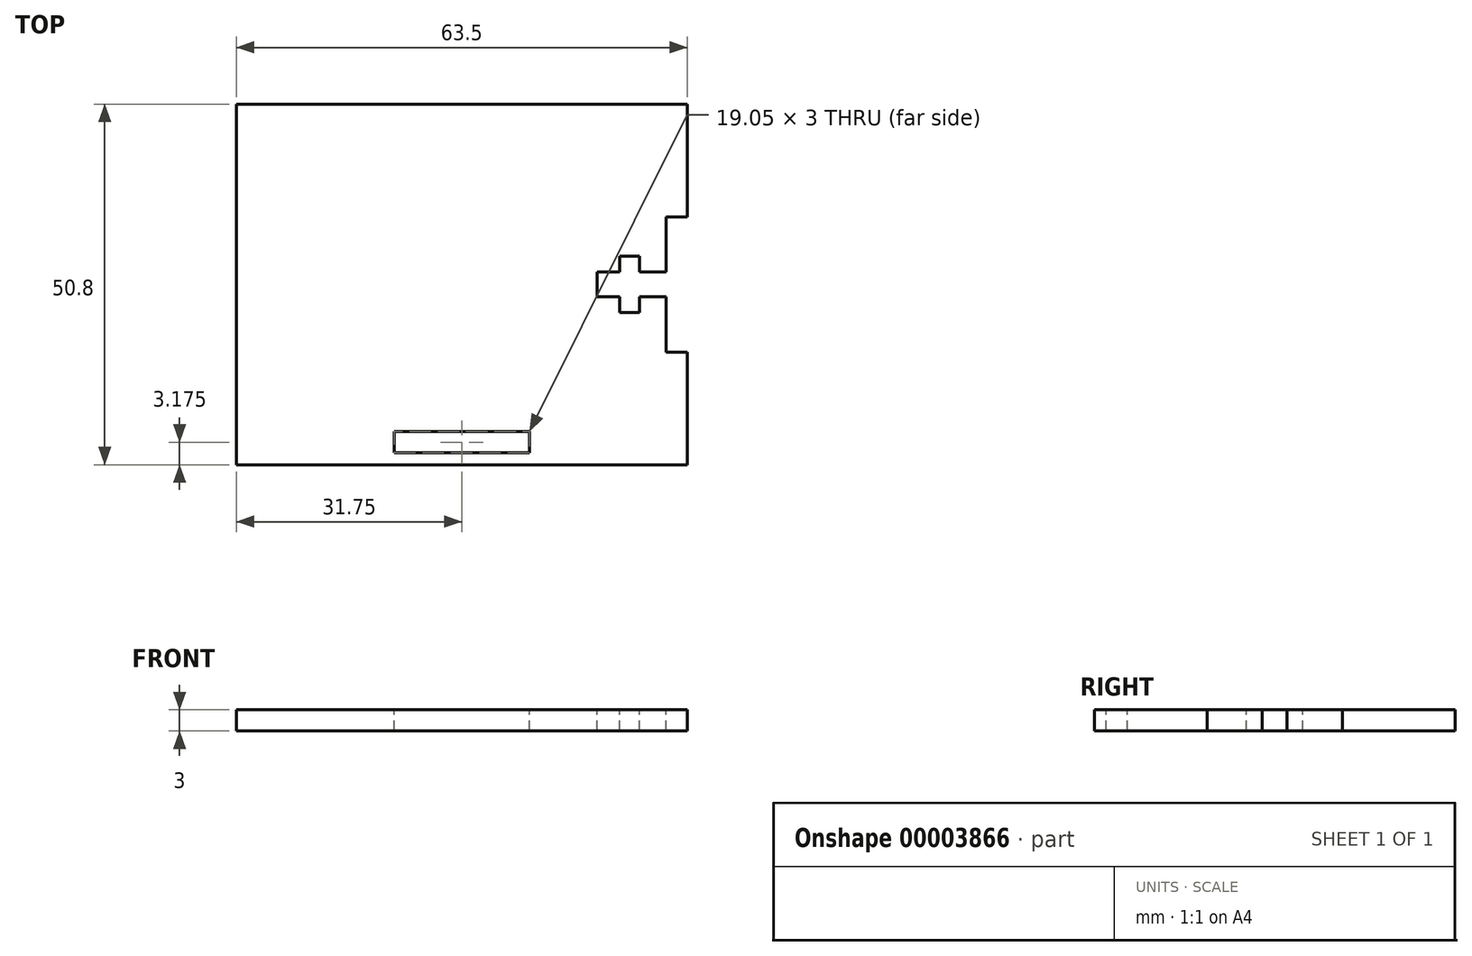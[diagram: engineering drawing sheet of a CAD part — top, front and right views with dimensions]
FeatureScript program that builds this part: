
annotation { "Feature Type Name" : "Feature", "Feature Type Description" : "" }
export const myFeature = defineFeature(function(context is Context, id is Id, definition is map)
    precondition{}
    {
        {
            var Q0;
            Q0=qCreatedBy(makeId("Top.planeOp"),FACE);
            var sketch = newSketch(context, id + "F0", { "sketchPlane" : qUnion([Q0])});
            skLineSegment(sketch, "E0.rect.bottom", {"start": v(31.75, 25.4) * mm, "end": v(-31.75, 25.4) * mm});
            skLineSegment(sketch, "E0.rect.top", {"start": v(31.75, -25.4) * mm, "end": v(-31.75, -25.4) * mm});
            skLineSegment(sketch, "E0.rect.left", {"start": v(31.75, 25.4) * mm, "end": v(31.75, -25.4) * mm});
            skLineSegment(sketch, "E0.rect.right", {"start": v(-31.75, 25.4) * mm, "end": v(-31.75, -25.4) * mm});
            skPoint(sketch, "E0.rect.middle", {"position": v(0, 0) * mm});
            skSolve(sketch);
        }
        {
            var Q0;
            Q0=makeQuery(id+"F0.imprint","IMPRINT",FACE,{"disambiguationData":[TD([[makeQuery(id+"F0.imprint","IMPRINT",EDGE,{"derivedFrom":sQuery(id+"F0.wireOp",EDGE,"E0.rect.bottom")}),1.0]])]});
            extrude(context, id + "F1", {"entities" : qUnion([Q0]), "depth" : 3 * mm});
        }
        {
            var Q0;
            Q0=makeQuery(id+"F1.opExtrude","CAP_FACE",FACE,{"disambiguationData":[OSD([sQuery(id+"F0.wireOp",EDGE,"E0.rect.bottom"),sQuery(id+"F0.wireOp",EDGE,"E0.rect.top"),sQuery(id+"F0.wireOp",EDGE,"E0.rect.left"),sQuery(id+"F0.wireOp",EDGE,"E0.rect.right")])],"isStart":false});
            var sketch = newSketch(context, id + "F2", { "sketchPlane" : qUnion([Q0])});
            skLineSegment(sketch, "E1.rect.bottom", {"start": v(9.53, -20.73) * mm, "end": v(-9.53, -20.73) * mm});
            skLineSegment(sketch, "E1.rect.top", {"start": v(9.53, -23.72) * mm, "end": v(-9.53, -23.72) * mm});
            skLineSegment(sketch, "E1.rect.left", {"start": v(9.53, -20.73) * mm, "end": v(9.53, -23.72) * mm});
            skLineSegment(sketch, "E1.rect.right", {"start": v(-9.53, -20.73) * mm, "end": v(-9.53, -23.72) * mm});
            skPoint(sketch, "E1.rect.middle", {"position": v(0, -22.23) * mm});
            skLineSegment(sketch, "E2.rect.bottom", {"start": v(28.75, 9.53) * mm, "end": v(31.75, 9.53) * mm});
            skLineSegment(sketch, "E2.rect.top", {"start": v(28.75, -9.53) * mm, "end": v(31.75, -9.53) * mm});
            skLineSegment(sketch, "E2.rect.right", {"start": v(31.75, 9.52) * mm, "end": v(31.75, -9.53) * mm});
            skPoint(sketch, "E2.rect.middle", {"position": v(30.25, 0) * mm});
            skLineSegment(sketch, "E3", {"start": v(28.75, 9.53) * mm, "end": v(28.75, 1.75) * mm});
            skLineSegment(sketch, "E4", {"start": v(28.75, 1.75) * mm, "end": v(25, 1.75) * mm});
            skLineSegment(sketch, "E5", {"start": v(25, 1.75) * mm, "end": v(25, 3.97) * mm});
            skLineSegment(sketch, "E6", {"start": v(25, 3.97) * mm, "end": v(22.22, 3.97) * mm});
            skLineSegment(sketch, "E7", {"start": v(22.22, 3.97) * mm, "end": v(22.22, 1.75) * mm});
            skLineSegment(sketch, "E8", {"start": v(22.22, 1.75) * mm, "end": v(19.05, 1.75) * mm});
            skLineSegment(sketch, "E9", {"start": v(19.05, 1.75) * mm, "end": v(19.05, 0) * mm});
            skLineSegment(sketch, "E10", {"start": v(31.75, 0) * mm, "end": v(11.15, 0) * mm, "construction": true});
            skLineSegment(sketch, "E11.0.MirrorCS", {"start": v(28.75, -9.53) * mm, "end": v(28.75, -1.75) * mm});
            skLineSegment(sketch, "E12.0.MirrorCS", {"start": v(28.75, -1.75) * mm, "end": v(25, -1.75) * mm});
            skLineSegment(sketch, "E13.0.MirrorCS", {"start": v(25, -1.75) * mm, "end": v(25, -3.97) * mm});
            skLineSegment(sketch, "E14.0.MirrorCS", {"start": v(25, -3.97) * mm, "end": v(22.22, -3.97) * mm});
            skLineSegment(sketch, "E15.0.MirrorCS", {"start": v(22.22, -3.97) * mm, "end": v(22.22, -1.75) * mm});
            skLineSegment(sketch, "E16.0.MirrorCS", {"start": v(22.22, -1.75) * mm, "end": v(19.05, -1.75) * mm});
            skLineSegment(sketch, "E17.0.MirrorCS", {"start": v(19.05, -1.75) * mm, "end": v(19.05, 0) * mm});
            skSolve(sketch);
        }
        {
            var Q0;
            {Q0=qUnion([makeQuery(id+"F2.imprint","IMPRINT",FACE,{"disambiguationData":[TD([[makeQuery(id+"F2.imprint","IMPRINT",EDGE,{"derivedFrom":sQuery(id+"F2.wireOp",EDGE,"E1.rect.bottom")}),1.0]])]}),makeQuery(id+"F2.imprint","IMPRINT",FACE,{"disambiguationData":[TD([[makeQuery(id+"F2.imprint","IMPRINT",EDGE,{"derivedFrom":sQuery(id+"F2.wireOp",EDGE,"E2.rect.bottom")}),-1.0]])]})]);}
            extrude(context, id + "F3", {"entities" : qUnion([Q0]), "operationType" : NewBodyOperationType.REMOVE, "oppositeDirection" : true, "depth" : 25.4 * mm});
        }
    });
